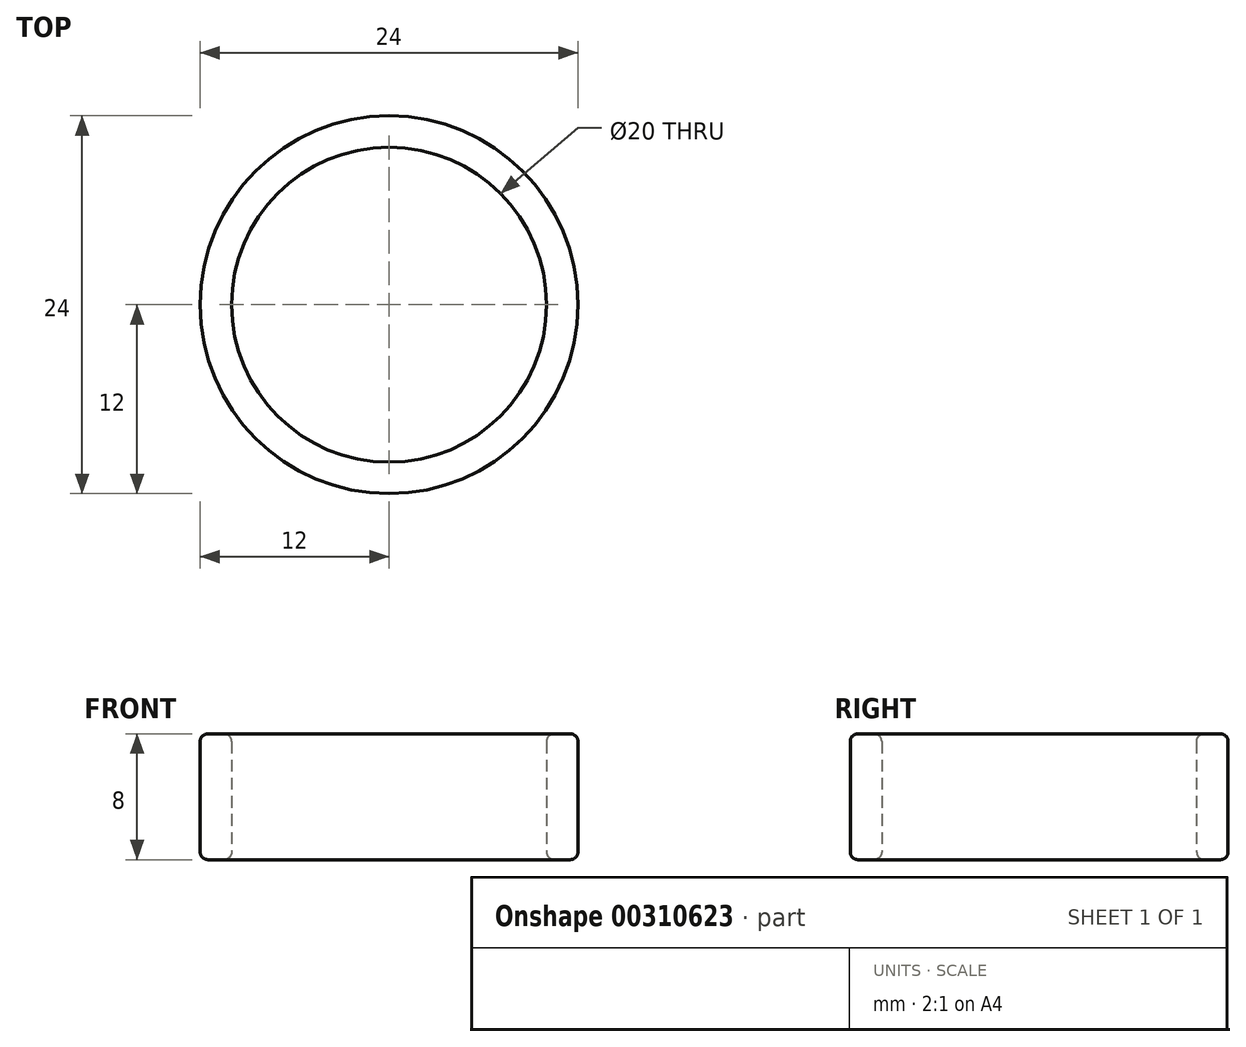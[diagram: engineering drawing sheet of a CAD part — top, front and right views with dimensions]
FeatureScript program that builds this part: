
annotation { "Feature Type Name" : "Feature", "Feature Type Description" : "" }
export const myFeature = defineFeature(function(context is Context, id is Id, definition is map)
    precondition{}
    {
        {
            var Q0;
            Q0=qCreatedBy(makeId("Top.planeOp"),FACE);
            var sketch = newSketch(context, id + "F0", { "sketchPlane" : qUnion([Q0])});
            skCircle(sketch, "E0", {"center": v(0, 0) * mm, "radius": 12 * mm});
            skCircle(sketch, "E1", {"center": v(0, 0) * mm, "radius": 10 * mm});
            skSolve(sketch);
        }
        {
            var Q0;
            Q0=makeQuery(id+"F0.imprint","IMPRINT",FACE,{"disambiguationData":[TD([[makeQuery(id+"F0.imprint","IMPRINT",EDGE,{"derivedFrom":sQuery(id+"F0.wireOp",EDGE,"E0")}),1.0]])]});
            extrude(context, id + "F1", {"entities" : qUnion([Q0]), "endBound" : BoundingType.SYMMETRIC, "depth" : 8 * mm});
        }
        {
            var Q0;
            Q0=makeQuery(id+"F1.opExtrude","CAP_EDGE",EDGE,{"disambiguationData":[OSD([sQuery(id+"F0.wireOp",EDGE,"E0")])],"isStart":false});
            var Q1;
            Q1=makeQuery(id+"F1.opExtrude","CAP_EDGE",EDGE,{"disambiguationData":[OSD([sQuery(id+"F0.wireOp",EDGE,"E1")])],"isStart":false});
            var Q2;
            Q2=makeQuery(id+"F1.opExtrude","CAP_EDGE",EDGE,{"disambiguationData":[OSD([sQuery(id+"F0.wireOp",EDGE,"E0")])],"isStart":true});
            var Q3;
            Q3=makeQuery(id+"F1.opExtrude","CAP_EDGE",EDGE,{"disambiguationData":[OSD([sQuery(id+"F0.wireOp",EDGE,"E1")])],"isStart":true});
            fillet(context, id + "F2", {"entities" : qUnion([Q0, Q1, Q2, Q3]), "radius" : 0.5 * mm, "tangentPropagation" : true, "allowEdgeOverflow" : false});
        }
    });
